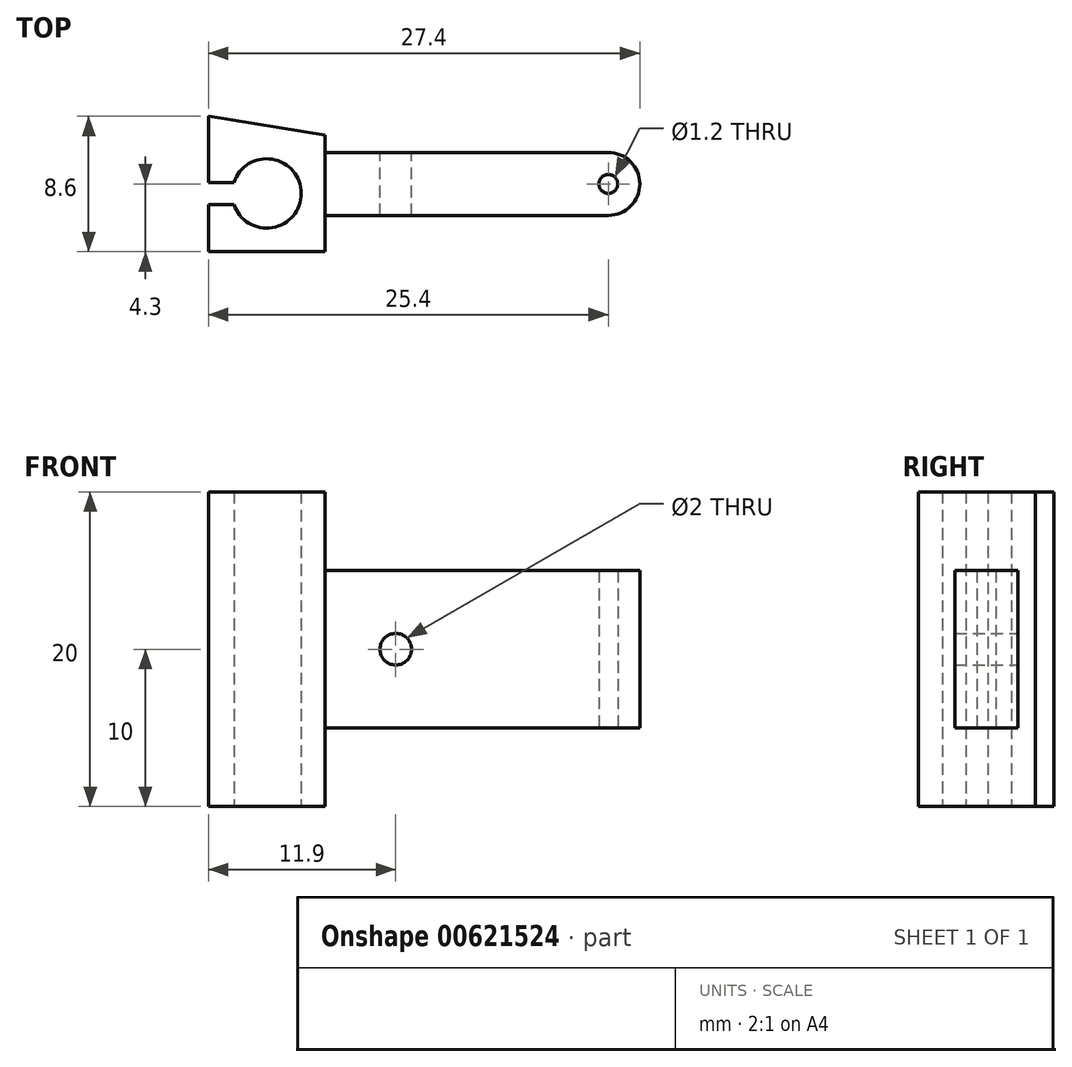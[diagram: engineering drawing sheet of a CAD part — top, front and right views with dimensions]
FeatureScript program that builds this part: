
annotation { "Feature Type Name" : "Feature", "Feature Type Description" : "" }
export const myFeature = defineFeature(function(context is Context, id is Id, definition is map)
    precondition{}
    {
        {
            var Q0;
            Q0=qCreatedBy(makeId("Top.planeOp"),FACE);
            var sketch = newSketch(context, id + "F0", { "sketchPlane" : qUnion([Q0])});
            skArc(sketch, "E0", {"start": v(-2.09, -0.7) * mm, "mid": v(2.2, 0) * mm, "end": v(-2.09, 0.7) * mm});
            skLineSegment(sketch, "E1.bottom", {"start": v(3.7, -3.7) * mm, "end": v(-3.7, -3.7) * mm});
            skLineSegment(sketch, "E1.left", {"start": v(3.7, -3.7) * mm, "end": v(3.7, -1.4) * mm});
            skLineSegment(sketch, "E2", {"start": v(-3.7, -3.7) * mm, "end": v(-3.7, -0.7) * mm});
            skLineSegment(sketch, "E3", {"start": v(-3.7, 4.9) * mm, "end": v(3.7, 3.7) * mm});
            skLineSegment(sketch, "E4.bottom", {"start": v(-3.7, -0.7) * mm, "end": v(-2.09, -0.7) * mm});
            skLineSegment(sketch, "E4.top", {"start": v(-3.7, 0.7) * mm, "end": v(-2.09, 0.7) * mm});
            skLineSegment(sketch, "E5.trimOffspring", {"start": v(-3.7, 0.7) * mm, "end": v(-3.7, 4.9) * mm});
            skLineSegment(sketch, "E6.bottom", {"start": v(3.7, -1.4) * mm, "end": v(21.7, -1.4) * mm});
            skLineSegment(sketch, "E6.top", {"start": v(3.7, 2.6) * mm, "end": v(21.7, 2.6) * mm});
            skLineSegment(sketch, "E6.right", {"start": v(23.7, 0.6) * mm, "end": v(23.7, 0.6) * mm});
            skLineSegment(sketch, "E7.trimOffspring", {"start": v(3.7, 2.6) * mm, "end": v(3.7, 3.7) * mm});
            skPoint(sketch, "E8.visualSharp", {"position": v(23.7, -1.4) * mm});
            skArc(sketch, "E8.filletArc", {"start": v(21.7, -1.4) * mm, "mid": v(23.11, -0.81) * mm, "end": v(23.7, 0.6) * mm});
            skPoint(sketch, "E9.visualSharp", {"position": v(23.7, 2.6) * mm});
            skArc(sketch, "E9.filletArc", {"start": v(23.7, 0.6) * mm, "mid": v(23.11, 2.01) * mm, "end": v(21.7, 2.6) * mm});
            skCircle(sketch, "E10", {"center": v(21.7, 0.6) * mm, "radius": 0.6 * mm});
            skSolve(sketch);
        }
        {
            var Q0;
            Q0=makeQuery(id+"F0.imprint","IMPRINT",FACE,{"disambiguationData":[TD([[makeQuery(id+"F0.imprint","IMPRINT",EDGE,{"derivedFrom":sQuery(id+"F0.wireOp",EDGE,"E0")}),-1.0]])]});
            extrude(context, id + "F1", {"entities" : qUnion([Q0]), "depth" : 20 * mm, "offsetDistance" : 25 * mm});
        }
        {
            var Q0;
            Q0=makeQuery(id+"F1.opExtrude","SWEPT_FACE",FACE,{"disambiguationData":[OSD([sQuery(id+"F0.wireOp",EDGE,"E6.bottom")])]});
            var sketch = newSketch(context, id + "F2", { "sketchPlane" : qUnion([Q0])});
            skLineSegment(sketch, "E11.bottom", {"start": v(3.7, 20) * mm, "end": v(23.7, 20) * mm});
            skLineSegment(sketch, "E11.top", {"start": v(3.7, 15) * mm, "end": v(23.7, 15) * mm});
            skLineSegment(sketch, "E11.left", {"start": v(3.7, 20) * mm, "end": v(3.7, 15) * mm});
            skLineSegment(sketch, "E11.right", {"start": v(23.7, 20) * mm, "end": v(23.7, 15) * mm});
            skLineSegment(sketch, "E12.bottom", {"start": v(3.7, 0) * mm, "end": v(23.7, 0) * mm});
            skLineSegment(sketch, "E12.top", {"start": v(3.7, 5) * mm, "end": v(23.7, 5) * mm});
            skLineSegment(sketch, "E12.left", {"start": v(3.7, 0) * mm, "end": v(3.7, 5) * mm});
            skLineSegment(sketch, "E12.right", {"start": v(23.7, 0) * mm, "end": v(23.7, 5) * mm});
            skSolve(sketch);
        }
        {
            var Q0;
            {var subQ0=sQuery(id+"F2.wireOp",EDGE,"E12.left");Q0=makeQuery(id+"F2.imprint","IMPRINT",FACE,{"disambiguationData":[TD([[makeQuery(id+"F2.imprint","IMPRINT",EDGE,{"derivedFrom":subQ0}),1.0]])]});}
            var Q1;
            {var subQ3=sQuery(id+"F2.wireOp",EDGE,"E12.right");Q1=makeQuery(id+"F2.imprint","IMPRINT",FACE,{"disambiguationData":[TD([[makeQuery(id+"F2.imprint","IMPRINT",EDGE,{"derivedFrom":subQ3}),1.0]])]});}
            var Q2;
            {var subQ3=sQuery(id+"F2.wireOp",EDGE,"E11.right");Q2=makeQuery(id+"F2.imprint","IMPRINT",FACE,{"disambiguationData":[TD([[makeQuery(id+"F2.imprint","IMPRINT",EDGE,{"derivedFrom":subQ3}),-1.0]])]});}
            var Q3;
            {var subQ0=sQuery(id+"F2.wireOp",EDGE,"E11.left");Q3=makeQuery(id+"F2.imprint","IMPRINT",FACE,{"disambiguationData":[TD([[makeQuery(id+"F2.imprint","IMPRINT",EDGE,{"derivedFrom":subQ0}),1.0]])]});}
            extrude(context, id + "F3", {"entities" : qUnion([Q0, Q1, Q2, Q3]), "operationType" : NewBodyOperationType.REMOVE, "oppositeDirection" : true, "depth" : 4 * mm, "offsetDistance" : 25 * mm});
        }
        {
            var Q0;
            Q0=makeQuery(id+"F1.opExtrude","SWEPT_FACE",FACE,{"disambiguationData":[OSD([sQuery(id+"F0.wireOp",EDGE,"E6.top")])]});
            var sketch = newSketch(context, id + "F4", { "sketchPlane" : qUnion([Q0])});
            skCircle(sketch, "E13", {"center": v(-8.2, 10) * mm, "radius": 1 * mm});
            skPoint(sketch, "E13.centerSnap0", {"position": v(-3.7, 10) * mm});
            skSolve(sketch);
        }
        {
            var Q0;
            Q0=makeQuery(id+"F4.imprint","IMPRINT",FACE,{"disambiguationData":[TD([[makeQuery(id+"F4.imprint","IMPRINT",EDGE,{"derivedFrom":sQuery(id+"F4.wireOp",EDGE,"E13")}),1.0]])]});
            extrude(context, id + "F5", {"entities" : qUnion([Q0]), "operationType" : NewBodyOperationType.REMOVE, "oppositeDirection" : true, "depth" : 4 * mm, "offsetDistance" : 25 * mm});
        }
    });
